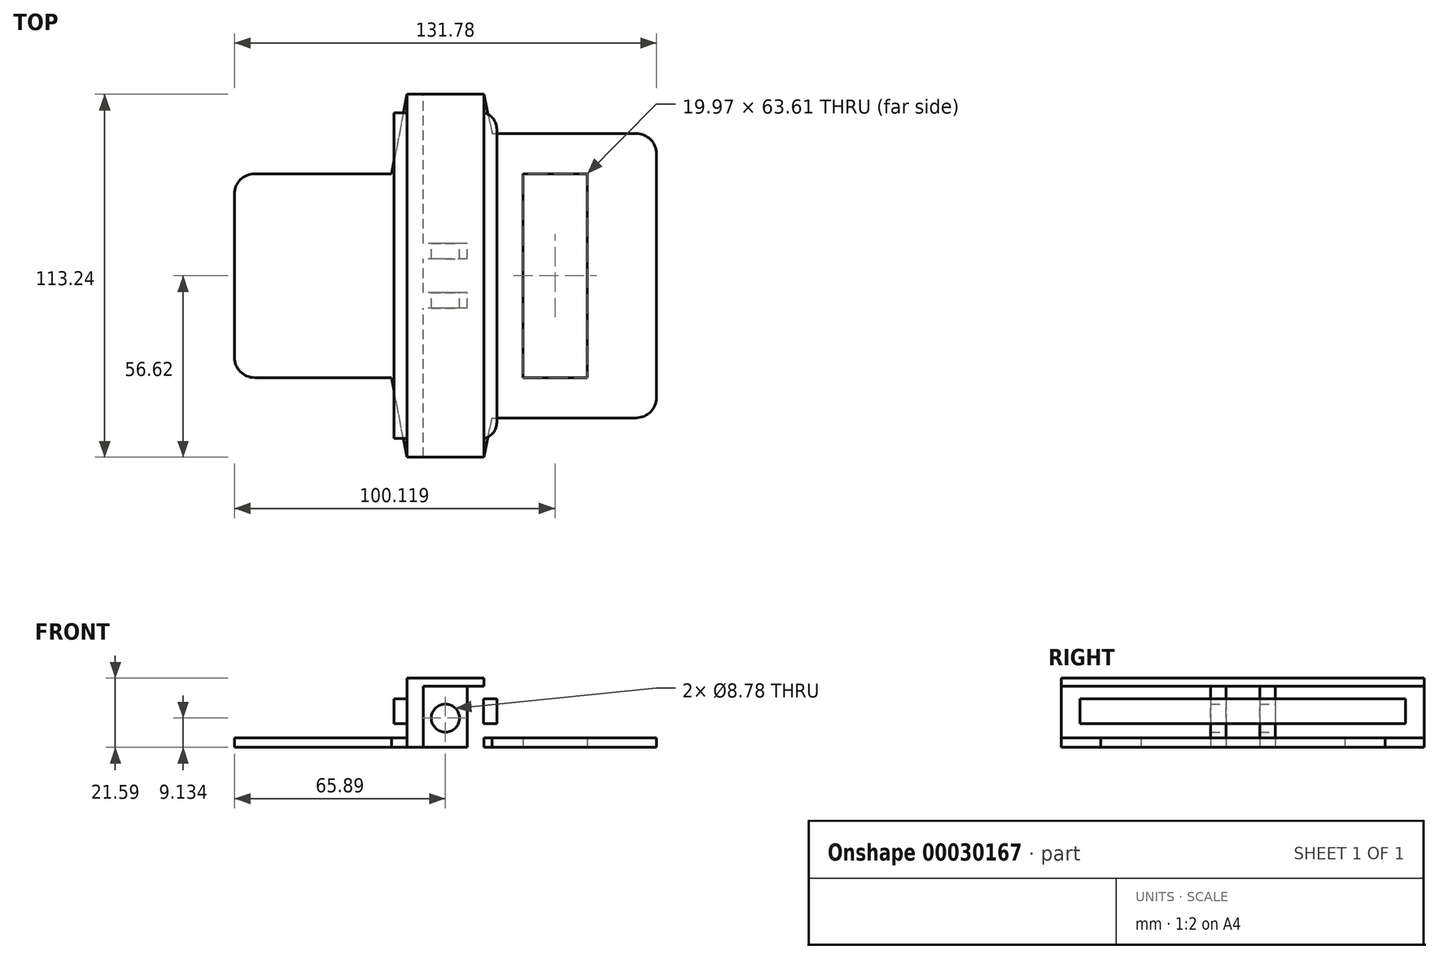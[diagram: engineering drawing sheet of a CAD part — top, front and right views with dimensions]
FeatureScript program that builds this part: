
annotation { "Feature Type Name" : "Feature", "Feature Type Description" : "" }
export const myFeature = defineFeature(function(context is Context, id is Id, definition is map)
    precondition{}
    {
        {
            var Q0;
            Q0=qCreatedBy(makeId("Top.planeOp"),FACE);
            var sketch = newSketch(context, id + "F0", { "sketchPlane" : qUnion([Q0])});
            skLineSegment(sketch, "E0.rect.bottom", {"start": v(44.21, -31.8) * mm, "end": v(24.25, -31.8) * mm});
            skLineSegment(sketch, "E0.rect.top", {"start": v(44.21, 31.8) * mm, "end": v(24.25, 31.8) * mm});
            skLineSegment(sketch, "E0.rect.left", {"start": v(65.9, -31.8) * mm, "end": v(65.9, 31.8) * mm});
            skLineSegment(sketch, "E0.rect.right", {"start": v(-65.9, -25.45) * mm, "end": v(-65.9, 25.45) * mm});
            skPoint(sketch, "E0.rect.middle", {"position": v(0, 0) * mm});
            skLineSegment(sketch, "E1.rect.bottom", {"start": v(12, 56.62) * mm, "end": v(-12, 56.62) * mm});
            skLineSegment(sketch, "E1.rect.top", {"start": v(12, -56.62) * mm, "end": v(-12, -56.62) * mm});
            skLineSegment(sketch, "E1.rect.left", {"start": v(12, 56.62) * mm, "end": v(12, -56.62) * mm});
            skLineSegment(sketch, "E1.rect.right", {"start": v(-12, 56.62) * mm, "end": v(-12, -56.62) * mm});
            skLineSegment(sketch, "E2.bottom", {"start": v(14.57, 44.35) * mm, "end": v(59.54, 44.35) * mm});
            skLineSegment(sketch, "E2.top", {"start": v(14.57, -44.35) * mm, "end": v(59.54, -44.35) * mm});
            skLineSegment(sketch, "E2.left", {"start": v(12, 44.35) * mm, "end": v(12, -44.35) * mm});
            skLineSegment(sketch, "E2.right", {"start": v(65.9, 38) * mm, "end": v(65.9, -38) * mm});
            skPoint(sketch, "E3.visualSharp", {"position": v(-65.9, 31.8) * mm});
            skArc(sketch, "E3.filletArc", {"start": v(-59.54, 31.8) * mm, "mid": v(-64.03, 29.94) * mm, "end": v(-65.9, 25.45) * mm});
            skPoint(sketch, "E4.visualSharp", {"position": v(65.9, 44.35) * mm});
            skArc(sketch, "E4.filletArc", {"start": v(65.9, 38) * mm, "mid": v(64.03, 42.5) * mm, "end": v(59.54, 44.35) * mm});
            skPoint(sketch, "E5.visualSharp", {"position": v(65.9, -44.35) * mm});
            skArc(sketch, "E5.filletArc", {"start": v(59.54, -44.35) * mm, "mid": v(64.03, -42.5) * mm, "end": v(65.9, -38) * mm});
            skPoint(sketch, "E6.visualSharp", {"position": v(-65.9, -31.8) * mm});
            skArc(sketch, "E6.filletArc", {"start": v(-65.9, -25.45) * mm, "mid": v(-64.03, -29.94) * mm, "end": v(-59.54, -31.8) * mm});
            skLineSegment(sketch, "E7.rect.left", {"start": v(44.21, -31.8) * mm, "end": v(44.21, 31.8) * mm});
            skLineSegment(sketch, "E7.rect.right", {"start": v(24.25, -31.8) * mm, "end": v(24.25, 31.8) * mm});
            skPoint(sketch, "E7.rect.middle", {"position": v(34.23, 0) * mm});
            skLineSegment(sketch, "E8", {"start": v(-12, 56.62) * mm, "end": v(-16.83, 31.8) * mm});
            skLineSegment(sketch, "E9", {"start": v(12, 56.62) * mm, "end": v(14.57, 44.35) * mm});
            skLineSegment(sketch, "E10", {"start": v(-6.85, 0) * mm, "end": v(6.85, 0) * mm});
            skLineSegment(sketch, "E11.MirrorCS", {"start": v(-12, -56.62) * mm, "end": v(-16.83, -31.8) * mm});
            skLineSegment(sketch, "E12.MirrorCS", {"start": v(12, -56.62) * mm, "end": v(14.57, -44.35) * mm});
            skLineSegment(sketch, "E13.rect.bottom", {"start": v(6.85, -56.62) * mm, "end": v(-6.85, -56.62) * mm});
            skLineSegment(sketch, "E13.rect.top", {"start": v(6.85, 56.62) * mm, "end": v(-6.85, 56.62) * mm});
            skLineSegment(sketch, "E13.rect.left", {"start": v(6.85, -56.62) * mm, "end": v(6.85, 56.62) * mm});
            skLineSegment(sketch, "E13.rect.right", {"start": v(-6.85, -56.62) * mm, "end": v(-6.85, 56.62) * mm});
            skLineSegment(sketch, "E14.rect.bottom", {"start": v(6.85, 5.28) * mm, "end": v(-6.85, 5.28) * mm});
            skLineSegment(sketch, "E14.rect.top", {"start": v(6.85, -5.28) * mm, "end": v(-6.85, -5.28) * mm});
            skLineSegment(sketch, "E14.rect.left", {"start": v(6.85, 5.28) * mm, "end": v(6.85, -5.28) * mm});
            skLineSegment(sketch, "E14.rect.right", {"start": v(-6.85, 5.28) * mm, "end": v(-6.85, -5.28) * mm});
            skLineSegment(sketch, "E15.rect.bottom", {"start": v(6.85, 10.13) * mm, "end": v(-6.85, 10.13) * mm});
            skLineSegment(sketch, "E15.rect.top", {"start": v(6.85, -10.13) * mm, "end": v(-6.85, -10.13) * mm});
            skLineSegment(sketch, "E15.rect.left", {"start": v(6.85, 10.13) * mm, "end": v(6.85, -10.13) * mm});
            skLineSegment(sketch, "E15.rect.right", {"start": v(-6.85, 10.13) * mm, "end": v(-6.85, -10.13) * mm});
            skLineSegment(sketch, "E16.trimOffspring", {"start": v(-16.83, 31.8) * mm, "end": v(-59.54, 31.8) * mm});
            skPoint(sketch, "E17.orphan", {"position": v(-12, 0) * mm});
            skPoint(sketch, "E18.orphan", {"position": v(12, 0) * mm});
            skLineSegment(sketch, "E19.trimOffspring", {"start": v(-16.83, -31.8) * mm, "end": v(-59.54, -31.8) * mm});
            skSolve(sketch);
        }
        {
            var Q0;
            Q0=makeQuery(id+"F0.imprint","IMPRINT",FACE,{"disambiguationData":[TD([[makeQuery(id+"F0.imprint","IMPRINT",EDGE,{"derivedFrom":sQuery(id+"F0.wireOp",EDGE,"E0.rect.right")}),-1.0]])]});
            var Q1;
            {var subQ11=sQuery(id+"F0.wireOp",EDGE,"E1.rect.right");Q1=makeQuery(id+"F0.imprint","IMPRINT",FACE,{"disambiguationData":[TD([[makeQuery(id+"F0.imprint","IMPRINT",EDGE,{"derivedFrom":subQ11}),1.0]])]});}
            var Q2;
            {var subQ11=sQuery(id+"F0.wireOp",EDGE,"E2.left");Q2=makeQuery(id+"F0.imprint","IMPRINT",FACE,{"disambiguationData":[TD([[makeQuery(id+"F0.imprint","IMPRINT",EDGE,{"derivedFrom":subQ11}),-1.0]])]});}
            var Q3;
            Q3=makeQuery(id+"F0.imprint","IMPRINT",FACE,{"disambiguationData":[TD([[makeQuery(id+"F0.imprint","IMPRINT",EDGE,{"derivedFrom":sQuery(id+"F0.wireOp",EDGE,"E2.bottom")}),-1.0]])]});
            extrude(context, id + "F1", {"entities" : qUnion([Q0, Q1, Q2, Q3]), "depth" : 3 * mm});
        }
        {
            var Q0;
            {var subQ11=sQuery(id+"F0.wireOp",EDGE,"E1.rect.right");Q0=makeQuery(id+"F0.imprint","IMPRINT",FACE,{"disambiguationData":[TD([[makeQuery(id+"F0.imprint","IMPRINT",EDGE,{"derivedFrom":subQ11}),1.0]])]});}
            var Q1;
            {var subQ11=sQuery(id+"F0.wireOp",EDGE,"E2.left");Q1=makeQuery(id+"F0.imprint","IMPRINT",FACE,{"disambiguationData":[TD([[makeQuery(id+"F0.imprint","IMPRINT",EDGE,{"derivedFrom":subQ11}),-1.0]])]});}
            var Q2;
            {var subQ2=sQuery(id+"F0.wireOp",EDGE,"E14.rect.bottom");Q2=makeQuery(id+"F0.imprint","IMPRINT",FACE,{"disambiguationData":[TD([[makeQuery(id+"F0.imprint","IMPRINT",EDGE,{"derivedFrom":subQ2}),-1.0]])]});}
            var Q3;
            {var subQ2=sQuery(id+"F0.wireOp",EDGE,"E14.rect.top");Q3=makeQuery(id+"F0.imprint","IMPRINT",FACE,{"disambiguationData":[TD([[makeQuery(id+"F0.imprint","IMPRINT",EDGE,{"derivedFrom":subQ2}),1.0]])]});}
            extrude(context, id + "F2", {"entities" : qUnion([Q0, Q1, Q2, Q3]), "operationType" : NewBodyOperationType.ADD, "depth" : 19.05 * mm});
        }
        {
            var Q0;
            Q0=makeQuery(id+"F2.opExtrude","CAP_FACE",FACE,{"disambiguationData":[OSD([sQuery(id+"F0.wireOp",EDGE,"E1.rect.bottom"),sQuery(id+"F0.wireOp",EDGE,"E1.rect.top"),sQuery(id+"F0.wireOp",EDGE,"E1.rect.right"),sQuery(id+"F0.wireOp",EDGE,"E13.rect.right"),sQuery(id+"F0.wireOp",EDGE,"E15.rect.right")])],"isStart":false});
            var sketch = newSketch(context, id + "F3", { "sketchPlane" : qUnion([Q0])});
            skLineSegment(sketch, "E20.rect.bottom", {"start": v(12, 56.62) * mm, "end": v(-12, 56.62) * mm});
            skLineSegment(sketch, "E20.rect.top", {"start": v(12, -56.62) * mm, "end": v(-12, -56.62) * mm});
            skLineSegment(sketch, "E20.rect.left", {"start": v(12, 56.62) * mm, "end": v(12, -56.62) * mm});
            skLineSegment(sketch, "E20.rect.right", {"start": v(-12, 56.62) * mm, "end": v(-12, -56.62) * mm});
            skPoint(sketch, "E20.rect.middle", {"position": v(0, 0) * mm});
            skSolve(sketch);
        }
        {
            var Q0;
            Q0 = qSketchRegion(id + "F3", true);
            extrude(context, id + "F4", {"entities" : qUnion([Q0]), "operationType" : NewBodyOperationType.ADD, "depth" : 2.54 * mm});
        }
        {
            var Q0;
            Q0=qCreatedBy(makeId("Front.planeOp"),FACE);
            var sketch = newSketch(context, id + "F5", { "sketchPlane" : qUnion([Q0])});
            skLineSegment(sketch, "E21.rect.bottom", {"start": v(16.03, 7.45) * mm, "end": v(-16.03, 7.45) * mm});
            skLineSegment(sketch, "E21.rect.top", {"start": v(16.03, 15.16) * mm, "end": v(-16.03, 15.16) * mm});
            skLineSegment(sketch, "E21.rect.left", {"start": v(16.03, 7.45) * mm, "end": v(16.03, 15.16) * mm});
            skLineSegment(sketch, "E21.rect.right", {"start": v(-16.03, 7.45) * mm, "end": v(-16.03, 15.16) * mm});
            skPoint(sketch, "E21.rect.middle", {"position": v(0, 11.3) * mm});
            skLineSegment(sketch, "E22.rect.bottom", {"start": v(11.95, 7.45) * mm, "end": v(-11.95, 7.45) * mm});
            skLineSegment(sketch, "E22.rect.top", {"start": v(11.95, 15.16) * mm, "end": v(-11.95, 15.16) * mm});
            skLineSegment(sketch, "E22.rect.left", {"start": v(11.95, 7.45) * mm, "end": v(11.95, 15.16) * mm});
            skLineSegment(sketch, "E22.rect.right", {"start": v(-11.95, 7.45) * mm, "end": v(-11.95, 15.16) * mm});
            skSolve(sketch);
        }
        {
            var Q0;
            {var subQ1=sQuery(id+"F5.wireOp",EDGE,"E21.rect.left");Q0=makeQuery(id+"F5.imprint","IMPRINT",FACE,{"disambiguationData":[TD([[makeQuery(id+"F5.imprint","IMPRINT",EDGE,{"derivedFrom":subQ1}),1.0]])]});}
            var Q1;
            {var subQ1=sQuery(id+"F5.wireOp",EDGE,"E21.rect.right");Q1=makeQuery(id+"F5.imprint","IMPRINT",FACE,{"disambiguationData":[TD([[makeQuery(id+"F5.imprint","IMPRINT",EDGE,{"derivedFrom":subQ1}),-1.0]])]});}
            extrude(context, id + "F6", {"entities" : qUnion([Q0, Q1]), "operationType" : NewBodyOperationType.ADD, "endBound" : BoundingType.SYMMETRIC, "depth" : 101.6 * mm});
        }
        {
            var Q0;
            Q0=makeQuery(id+"F1.opExtrude","SWEPT_EDGE",EDGE,{"disambiguationData":[OSD([sQuery(id+"F0.wireOp",EDGE,"E1.rect.bottom"),sQuery(id+"F0.wireOp",EDGE,"E1.rect.right"),sQuery(id+"F0.wireOp",EDGE,"E8")])]});
            var Q1;
            Q1=makeQuery(id+"F1.opExtrude","SWEPT_EDGE",EDGE,{"disambiguationData":[OSD([sQuery(id+"F0.wireOp",EDGE,"E1.rect.bottom"),sQuery(id+"F0.wireOp",EDGE,"E1.rect.left"),sQuery(id+"F0.wireOp",EDGE,"E9")])]});
            var Q2;
            Q2=makeQuery(id+"F1.opExtrude","SWEPT_EDGE",EDGE,{"disambiguationData":[OSD([sQuery(id+"F0.wireOp",EDGE,"E8"),sQuery(id+"F0.wireOp",EDGE,"E16.trimOffspring")])]});
            var Q3;
            Q3=makeQuery(id+"F1.opExtrude","SWEPT_EDGE",EDGE,{"disambiguationData":[OSD([sQuery(id+"F0.wireOp",EDGE,"E2.bottom"),sQuery(id+"F0.wireOp",EDGE,"E9")])]});
            var Q4;
            Q4=makeQuery(id+"F1.opExtrude","SWEPT_EDGE",EDGE,{"disambiguationData":[OSD([sQuery(id+"F0.wireOp",EDGE,"E11.MirrorCS"),sQuery(id+"F0.wireOp",EDGE,"E19.trimOffspring")])]});
            var Q5;
            Q5=makeQuery(id+"F1.opExtrude","SWEPT_EDGE",EDGE,{"disambiguationData":[OSD([sQuery(id+"F0.wireOp",EDGE,"E1.rect.top"),sQuery(id+"F0.wireOp",EDGE,"E1.rect.right"),sQuery(id+"F0.wireOp",EDGE,"E11.MirrorCS")])]});
            var Q6;
            Q6=makeQuery(id+"F1.opExtrude","SWEPT_EDGE",EDGE,{"disambiguationData":[OSD([sQuery(id+"F0.wireOp",EDGE,"E2.top"),sQuery(id+"F0.wireOp",EDGE,"E12.MirrorCS")])]});
            var Q7;
            Q7=makeQuery(id+"F1.opExtrude","SWEPT_EDGE",EDGE,{"disambiguationData":[OSD([sQuery(id+"F0.wireOp",EDGE,"E1.rect.top"),sQuery(id+"F0.wireOp",EDGE,"E1.rect.left"),sQuery(id+"F0.wireOp",EDGE,"E12.MirrorCS")])]});
            var Q8;
            Q8=makeQuery(id+"F1.opExtrude","SWEPT_EDGE",EDGE,{"disambiguationData":[OSD([sQuery(id+"F0.wireOp",EDGE,"E0.rect.top"),sQuery(id+"F0.wireOp",EDGE,"E7.rect.right")])]});
            var Q9;
            Q9=makeQuery(id+"F1.opExtrude","SWEPT_EDGE",EDGE,{"disambiguationData":[OSD([sQuery(id+"F0.wireOp",EDGE,"E0.rect.top"),sQuery(id+"F0.wireOp",EDGE,"E7.rect.left")])]});
            var Q10;
            Q10=makeQuery(id+"F1.opExtrude","SWEPT_EDGE",EDGE,{"disambiguationData":[OSD([sQuery(id+"F0.wireOp",EDGE,"E0.rect.bottom"),sQuery(id+"F0.wireOp",EDGE,"E7.rect.left")])]});
            var Q11;
            Q11=makeQuery(id+"F1.opExtrude","SWEPT_EDGE",EDGE,{"disambiguationData":[OSD([sQuery(id+"F0.wireOp",EDGE,"E0.rect.bottom"),sQuery(id+"F0.wireOp",EDGE,"E7.rect.right")])]});
            var Q12;
            Q12=makeQuery(id+"F4.boolean.opBoolean","MERGE",EDGE,{"derivedFrom":[makeQuery(id+"F2.opExtrude","SWEPT_EDGE",EDGE,{"disambiguationData":[OSD([sQuery(id+"F0.wireOp",EDGE,"E1.rect.top"),sQuery(id+"F0.wireOp",EDGE,"E1.rect.right"),sQuery(id+"F0.wireOp",EDGE,"E11.MirrorCS")])]}),makeQuery(id+"F4.opExtrude","SWEPT_EDGE",EDGE,{"disambiguationData":[OSD([sQuery(id+"F3.wireOp",EDGE,"E20.rect.top"),sQuery(id+"F3.wireOp",EDGE,"E20.rect.right")])]})]});
            var Q13;
            Q13=makeQuery(id+"F4.boolean.opBoolean","MERGE",EDGE,{"derivedFrom":[makeQuery(id+"F2.opExtrude","SWEPT_EDGE",EDGE,{"disambiguationData":[OSD([sQuery(id+"F0.wireOp",EDGE,"E1.rect.bottom"),sQuery(id+"F0.wireOp",EDGE,"E1.rect.right"),sQuery(id+"F0.wireOp",EDGE,"E8")])]}),makeQuery(id+"F4.opExtrude","SWEPT_EDGE",EDGE,{"disambiguationData":[OSD([sQuery(id+"F3.wireOp",EDGE,"E20.rect.bottom"),sQuery(id+"F3.wireOp",EDGE,"E20.rect.right")])]})]});
            var Q14;
            Q14=makeQuery(id+"F6.opExtrude","CAP_EDGE",EDGE,{"disambiguationData":[OSD([sQuery(id+"F5.wireOp",EDGE,"E21.rect.right")])],"isStart":false});
            var Q15;
            Q15=makeQuery(id+"F6.opExtrude","CAP_EDGE",EDGE,{"disambiguationData":[OSD([sQuery(id+"F5.wireOp",EDGE,"E21.rect.left")])],"isStart":false});
            var Q16;
            Q16=makeQuery(id+"F6.opExtrude","CAP_EDGE",EDGE,{"disambiguationData":[OSD([sQuery(id+"F5.wireOp",EDGE,"E21.rect.left")])],"isStart":true});
            var Q17;
            Q17=makeQuery(id+"F6.opExtrude","CAP_EDGE",EDGE,{"disambiguationData":[OSD([sQuery(id+"F5.wireOp",EDGE,"E21.rect.right")])],"isStart":true});
            fillet(context, id + "F7", {"entities" : qUnion([Q0, Q1, Q2, Q3, Q4, Q5, Q6, Q7, Q8, Q9, Q10, Q11, Q12, Q13, Q14, Q15, Q16, Q17]), "radius" : 5.08 * mm, "tangentPropagation" : true, "allowEdgeOverflow" : false});
        }
        {
            var Q0;
            Q0=makeQuery(id+"F2.opExtrude","SWEPT_FACE",FACE,{"disambiguationData":[OSD([sQuery(id+"F0.wireOp",EDGE,"E15.rect.bottom")])]});
            var sketch = newSketch(context, id + "F8", { "sketchPlane" : qUnion([Q0])});
            skCircle(sketch, "E23", {"center": v(0, 9.13) * mm, "radius": 4.4 * mm});
            skSolve(sketch);
        }
        {
            var Q0;
            Q0 = qSketchRegion(id + "F8", true);
            extrude(context, id + "F9", {"entities" : qUnion([Q0]), "operationType" : NewBodyOperationType.REMOVE, "endBound" : BoundingType.THROUGH_ALL, "oppositeDirection" : true, "depth" : 25.4 * mm});
        }
    });
